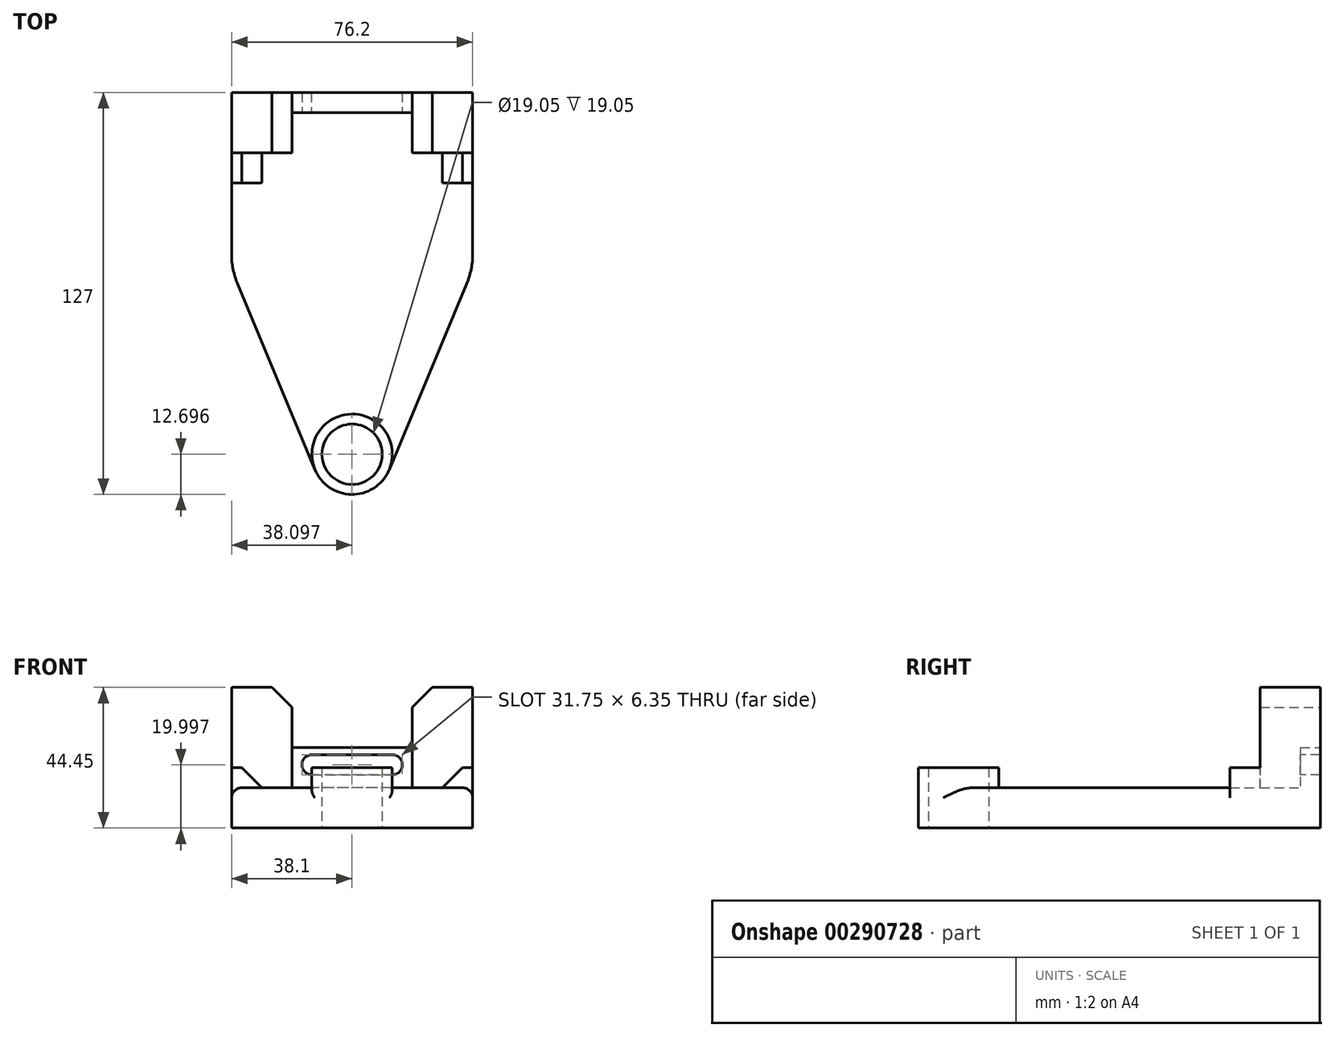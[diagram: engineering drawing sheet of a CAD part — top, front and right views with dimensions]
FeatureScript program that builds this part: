
annotation { "Feature Type Name" : "Feature", "Feature Type Description" : "" }
export const myFeature = defineFeature(function(context is Context, id is Id, definition is map)
    precondition{}
    {
        {
            var Q0;
            Q0=qCreatedBy(makeId("Top.planeOp"),FACE);
            var sketch = newSketch(context, id + "F0", { "sketchPlane" : qUnion([Q0])});
            skLineSegment(sketch, "E0", {"start": v(-21.93, 48.5) * mm, "end": v(54.27, 48.5) * mm});
            skLineSegment(sketch, "E1", {"start": v(54.27, 48.5) * mm, "end": v(54.27, -2.3) * mm});
            skLineSegment(sketch, "E2", {"start": v(-21.93, 48.5) * mm, "end": v(-21.93, -2.3) * mm});
            skLineSegment(sketch, "E3", {"start": v(-21.93, 29.46) * mm, "end": v(-2.88, 29.46) * mm});
            skLineSegment(sketch, "E4", {"start": v(-2.88, 29.46) * mm, "end": v(-2.88, 48.5) * mm});
            skLineSegment(sketch, "E5", {"start": v(35.22, 48.5) * mm, "end": v(35.22, 29.46) * mm});
            skLineSegment(sketch, "E6", {"start": v(35.22, 29.46) * mm, "end": v(54.27, 29.46) * mm});
            skCircle(sketch, "E7", {"center": v(16.17, -65.8) * mm, "radius": 12.7 * mm});
            skCircle(sketch, "E8", {"center": v(16.17, -65.8) * mm, "radius": 9.53 * mm});
            skLineSegment(sketch, "E9", {"start": v(-19.98, -12.06) * mm, "end": v(4.44, -70.68) * mm});
            skLineSegment(sketch, "E10", {"start": v(44.74, 29.46) * mm, "end": v(44.74, 19.93) * mm});
            skLineSegment(sketch, "E11", {"start": v(44.74, 19.93) * mm, "end": v(54.27, 19.93) * mm});
            skPoint(sketch, "E12.visualSharp", {"position": v(-21.93, -7.37) * mm});
            skArc(sketch, "E12.filletArc", {"start": v(-21.93, -2.3) * mm, "mid": v(-21.44, -7.28) * mm, "end": v(-19.98, -12.06) * mm});
            skLineSegment(sketch, "E13", {"start": v(27.89, -70.68) * mm, "end": v(52.31, -12.06) * mm});
            skPoint(sketch, "E14.visualSharp", {"position": v(54.27, -7.37) * mm});
            skArc(sketch, "E14.filletArc", {"start": v(52.31, -12.06) * mm, "mid": v(53.77, -7.28) * mm, "end": v(54.27, -2.3) * mm});
            skLineSegment(sketch, "E15", {"start": v(-12.4, 29.46) * mm, "end": v(-12.4, 19.93) * mm});
            skLineSegment(sketch, "E16", {"start": v(-12.4, 19.93) * mm, "end": v(-21.93, 19.93) * mm});
            skLineSegment(sketch, "E17", {"start": v(-2.88, 42.16) * mm, "end": v(35.22, 42.16) * mm});
            skLineSegment(sketch, "E18", {"start": v(16.17, 48.5) * mm, "end": v(16.17, -65.8) * mm, "construction": true});
            skSolve(sketch);
        }
        {
            var Q0;
            Q0 = qSketchRegion(id + "F0", true);
            extrude(context, id + "F1", {"entities" : qUnion([Q0]), "depth" : 12.7 * mm});
        }
        {
            var Q0;
            Q0=makeQuery(id+"F0.imprint","IMPRINT",FACE,{"disambiguationData":[TD([[makeQuery(id+"F0.imprint","IMPRINT",EDGE,{"derivedFrom":sQuery(id+"F0.wireOp",EDGE,"E8")}),1.0]])]});
            var Q1;
            Q1=makeQuery(id+"F0.imprint","IMPRINT",FACE,{"disambiguationData":[TD([[makeQuery(id+"F0.imprint","IMPRINT",EDGE,{"derivedFrom":sQuery(id+"F0.wireOp",EDGE,"E8")}),-1.0]])]});
            extrude(context, id + "F2", {"entities" : qUnion([Q0, Q1]), "operationType" : NewBodyOperationType.ADD, "depth" : 19.05 * mm});
        }
        {
            var Q0;
            {var subQ4=sQuery(id+"F0.wireOp",EDGE,"E15");Q0=makeQuery(id+"F0.imprint","IMPRINT",FACE,{"disambiguationData":[TD([[makeQuery(id+"F0.imprint","IMPRINT",EDGE,{"derivedFrom":subQ4}),-1.0]])]});}
            var Q1;
            {var subQ4=sQuery(id+"F0.wireOp",EDGE,"E10");Q1=makeQuery(id+"F0.imprint","IMPRINT",FACE,{"disambiguationData":[TD([[makeQuery(id+"F0.imprint","IMPRINT",EDGE,{"derivedFrom":subQ4}),1.0]])]});}
            extrude(context, id + "F3", {"entities" : qUnion([Q0, Q1]), "operationType" : NewBodyOperationType.ADD, "depth" : 19.05 * mm});
        }
        {
            var Q0;
            {var subQ5=sQuery(id+"F0.wireOp",EDGE,"E17");Q0=makeQuery(id+"F0.imprint","IMPRINT",FACE,{"disambiguationData":[TD([[makeQuery(id+"F0.imprint","IMPRINT",EDGE,{"derivedFrom":subQ5}),1.0]])]});}
            extrude(context, id + "F4", {"entities" : qUnion([Q0]), "operationType" : NewBodyOperationType.ADD, "depth" : 25.4 * mm});
        }
        {
            var Q0;
            {var subQ1=sQuery(id+"F0.wireOp",EDGE,"E2");var subQ4=sQuery(id+"F0.wireOp",EDGE,"E0");var subQ5=makeQuery(id+"F0.imprint","INTERSECT",VERTEX,{"derivedFrom":[subQ4,subQ1]});Q0=makeQuery(id+"F0.imprint","IMPRINT",FACE,{"disambiguationData":[TD([[makeQuery(id+"F0.imprint","IMPRINT",EDGE,{"disambiguationData":[TD([[subQ5,-1.0]])],"derivedFrom":subQ4}),-1.0]])]});}
            var Q1;
            {var subQ4=sQuery(id+"F0.wireOp",EDGE,"E1");var subQ5=sQuery(id+"F0.wireOp",EDGE,"E0");var subQ6=makeQuery(id+"F0.imprint","INTERSECT",VERTEX,{"derivedFrom":[subQ5,subQ4]});Q1=makeQuery(id+"F0.imprint","IMPRINT",FACE,{"disambiguationData":[TD([[makeQuery(id+"F0.imprint","IMPRINT",EDGE,{"disambiguationData":[TD([[subQ6,1.0]])],"derivedFrom":subQ5}),-1.0]])]});}
            extrude(context, id + "F5", {"entities" : qUnion([Q0, Q1]), "operationType" : NewBodyOperationType.ADD, "depth" : 44.45 * mm});
        }
        {
            var Q0;
            Q0=makeQuery(id+"F4.opExtrude","SWEPT_FACE",FACE,{"disambiguationData":[OSD([sQuery(id+"F0.wireOp",EDGE,"E17")])]});
            var sketch = newSketch(context, id + "F6", { "sketchPlane" : qUnion([Q0])});
            skPoint(sketch, "E19", {"position": v(3.47, 20) * mm});
            skPoint(sketch, "E20", {"position": v(28.87, 20) * mm});
            skArc(sketch, "E21", {"start": v(3.7, 23.16) * mm, "mid": v(0.3, 20.1) * mm, "end": v(3.49, 16.82) * mm});
            skArc(sketch, "E22", {"start": v(28.87, 16.82) * mm, "mid": v(32.04, 20) * mm, "end": v(28.87, 23.17) * mm});
            skLineSegment(sketch, "E23", {"start": v(-2.88, 20.11) * mm, "end": v(0.3, 20.11) * mm, "construction": true});
            skLineSegment(sketch, "E24", {"start": v(32.04, 19.8) * mm, "end": v(35.22, 19.8) * mm, "construction": true});
            skLineSegment(sketch, "E25", {"start": v(3.24, 23.16) * mm, "end": v(28.87, 23.17) * mm});
            skLineSegment(sketch, "E26", {"start": v(3.49, 16.82) * mm, "end": v(28.87, 16.82) * mm});
            skLineSegment(sketch, "E27", {"start": v(3.47, 20) * mm, "end": v(28.87, 20) * mm, "construction": true});
            skSolve(sketch);
        }
        {
            var Q0;
            {var subQ3=sQuery(id+"F6.wireOp",EDGE,"E22");Q0=makeQuery(id+"F6.imprint","IMPRINT",FACE,{"disambiguationData":[TD([[makeQuery(id+"F6.imprint","IMPRINT",EDGE,{"derivedFrom":subQ3}),1.0]])]});}
            extrude(context, id + "F7", {"entities" : qUnion([Q0]), "operationType" : NewBodyOperationType.REMOVE, "oppositeDirection" : true, "depth" : 25.4 * mm});
        }
        {
            var Q0;
            Q0=makeQuery(id+"F5.opExtrude","CAP_EDGE",EDGE,{"disambiguationData":[OSD([sQuery(id+"F0.wireOp",EDGE,"E4")])],"isStart":false});
            var Q1;
            Q1=makeQuery(id+"F5.opExtrude","CAP_EDGE",EDGE,{"disambiguationData":[OSD([sQuery(id+"F0.wireOp",EDGE,"E5")])],"isStart":false});
            var Q2;
            Q2=makeQuery(id+"F3.opExtrude","CAP_EDGE",EDGE,{"disambiguationData":[OSD([sQuery(id+"F0.wireOp",EDGE,"E10")])],"isStart":false});
            var Q3;
            Q3=makeQuery(id+"F3.opExtrude","CAP_EDGE",EDGE,{"disambiguationData":[OSD([sQuery(id+"F0.wireOp",EDGE,"E15")])],"isStart":false});
            chamfer(context, id + "F8", {"entities" : qUnion([Q0, Q1, Q2, Q3]), "width" : 6.35 * mm, "tangentPropagation" : true});
        }
        {
            var Q0;
            Q0=makeQuery(id+"F1.opExtrude","CAP_EDGE",EDGE,{"disambiguationData":[OSD([sQuery(id+"F0.wireOp",EDGE,"E9")])],"isStart":false});
            var Q1;
            Q1=makeQuery(id+"F1.opExtrude","CAP_EDGE",EDGE,{"disambiguationData":[OSD([sQuery(id+"F0.wireOp",EDGE,"E13")])],"isStart":false});
            var Q2;
            Q2=makeQuery(id+"F1.opExtrude","CAP_EDGE",EDGE,{"disambiguationData":[OSD([sQuery(id+"F0.wireOp",EDGE,"E14.filletArc")])],"isStart":false});
            var Q3;
            {var subQ0=sQuery(id+"F0.wireOp",EDGE,"E2");var subQ1=sQuery(id+"F0.wireOp",EDGE,"E12.filletArc");Q3=makeQuery(id+"F3.boolean.opBoolean","SPLIT",EDGE,{"disambiguationData":[TD([makeQuery(id+"F1.opExtrude","SWEPT_FACE",FACE,{"disambiguationData":[OSD([subQ1])]})])],"derivedFrom":makeQuery(id+"F1.opExtrude","CAP_EDGE",EDGE,{"disambiguationData":[OSD([subQ0])],"isStart":false})});}
            var Q4;
            Q4=makeQuery(id+"F1.opExtrude","CAP_EDGE",EDGE,{"disambiguationData":[OSD([sQuery(id+"F0.wireOp",EDGE,"E12.filletArc")])],"isStart":false});
            var Q5;
            {var subQ0=sQuery(id+"F0.wireOp",EDGE,"E14.filletArc");var subQ1=sQuery(id+"F0.wireOp",EDGE,"E1");Q5=makeQuery(id+"F3.boolean.opBoolean","SPLIT",EDGE,{"disambiguationData":[TD([makeQuery(id+"F1.opExtrude","SWEPT_FACE",FACE,{"disambiguationData":[OSD([subQ0])]})])],"derivedFrom":makeQuery(id+"F1.opExtrude","CAP_EDGE",EDGE,{"disambiguationData":[OSD([subQ1])],"isStart":false})});}
            fillet(context, id + "F9", {"entities" : qUnion([Q0, Q1, Q2, Q3, Q4, Q5]), "radius" : 3.17 * mm, "tangentPropagation" : true, "allowEdgeOverflow" : false});
        }
        {
            var Q0;
            Q0=makeQuery(id+"F0.imprint","IMPRINT",FACE,{"disambiguationData":[TD([[makeQuery(id+"F0.imprint","IMPRINT",EDGE,{"derivedFrom":sQuery(id+"F0.wireOp",EDGE,"E8")}),1.0]])]});
            extrude(context, id + "F10", {"entities" : qUnion([Q0]), "operationType" : NewBodyOperationType.REMOVE, "depth" : 25.4 * mm});
        }
    });
